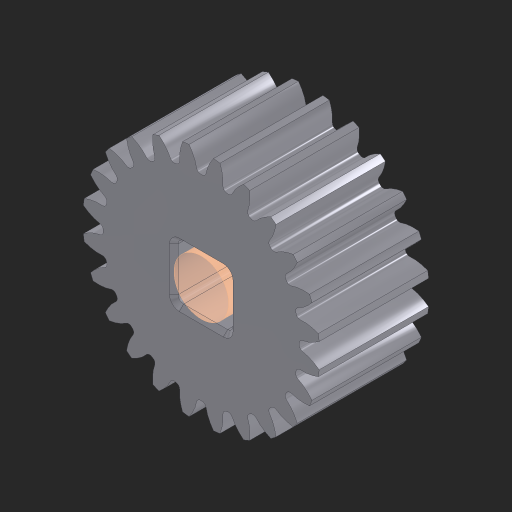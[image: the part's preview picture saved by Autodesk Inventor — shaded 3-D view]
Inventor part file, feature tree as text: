
AUTODESK INVENTOR PART (.ipt)
format: ipt  version: 2023 (Build 270158000, 158)  size: 350,208 bytes
history: native  units: in
note: dims shown in document units (in); Inventor stores cm internally (conversion verified against a paired STEP export)
features: sketch x1, other x1, chamfer x1, extrude x1
ambient origin geometry x8: Origin, YZ Plane, XZ Plane, XY Plane, X Axis, Y Axis, Z Axis, Center Point
bodies: Solid1 (feature_tree)
feature tree (4):
  sketch  "Sketch1"  dims[d0=0.25in d1=0.3937in d2=0.0in]
  other  "Srf1"
  chamfer  "Chamfer1"  Distance=0.3937in
  extrude  "ExtrusionSrf1"  [1 undecoded]
note: 1 required parameter value undecoded (feature->parameter linkage not recoverable at this tier; creation-order binding heuristic only, values carry confidence <= 0.55)
